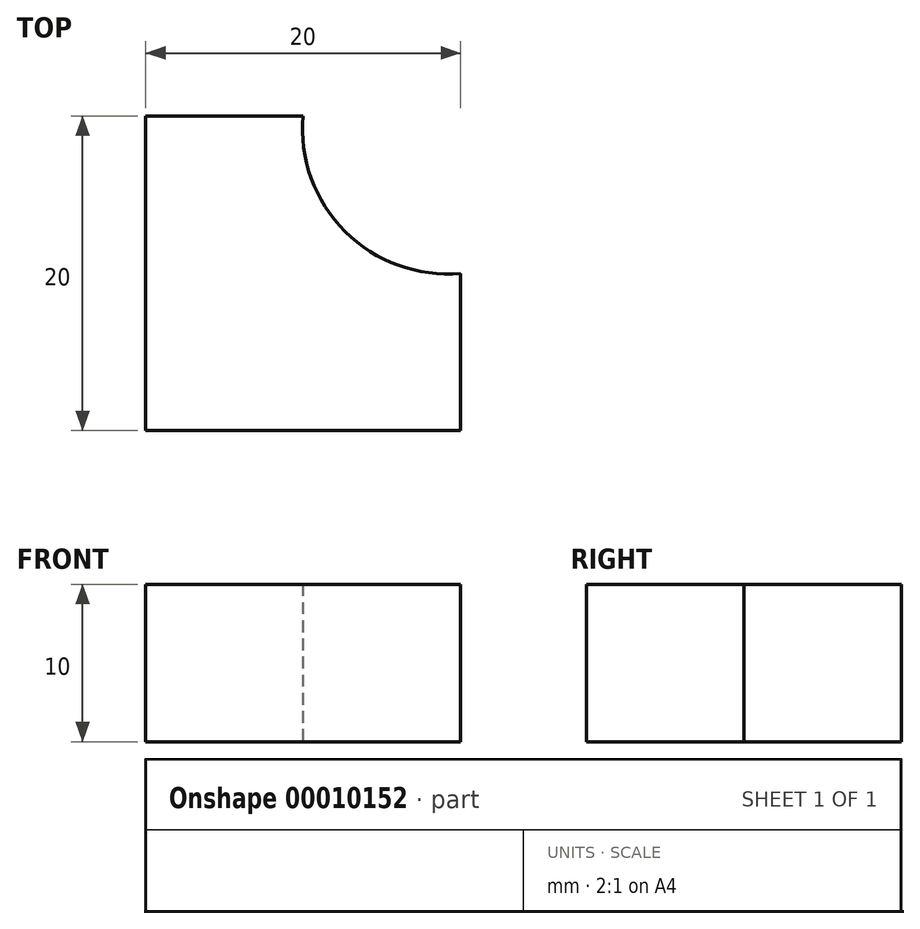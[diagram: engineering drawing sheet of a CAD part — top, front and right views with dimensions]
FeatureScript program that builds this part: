
annotation { "Feature Type Name" : "Feature", "Feature Type Description" : "" }
export const myFeature = defineFeature(function(context is Context, id is Id, definition is map)
    precondition{}
    {
        {
            var Q0;
            Q0=qCreatedBy(makeId("Top.planeOp"),FACE);
            var sketch = newSketch(context, id + "F0", { "sketchPlane" : qUnion([Q0])});
            skLineSegment(sketch, "E0", {"start": v(0, 0) * mm, "end": v(20, 0) * mm});
            skLineSegment(sketch, "E1", {"start": v(20, 0) * mm, "end": v(20, 10) * mm});
            skLineSegment(sketch, "E2", {"start": v(0, 0) * mm, "end": v(0, 20) * mm});
            skLineSegment(sketch, "E3", {"start": v(0, 20) * mm, "end": v(10, 20) * mm});
            skArc(sketch, "E4", {"start": v(10, 20) * mm, "mid": v(12.66, 12.66) * mm, "end": v(20, 10) * mm});
            skSolve(sketch);
        }
        {
            var Q0;
            Q0=makeQuery(id+"F0.imprint","IMPRINT",FACE,{"disambiguationData":[TD([[makeQuery(id+"F0.imprint","IMPRINT",EDGE,{"derivedFrom":sQuery(id+"F0.wireOp",EDGE,"E0")}),1.0]])]});
            extrude(context, id + "F1", {"entities" : qUnion([Q0]), "depth" : 10 * mm});
        }
    });
